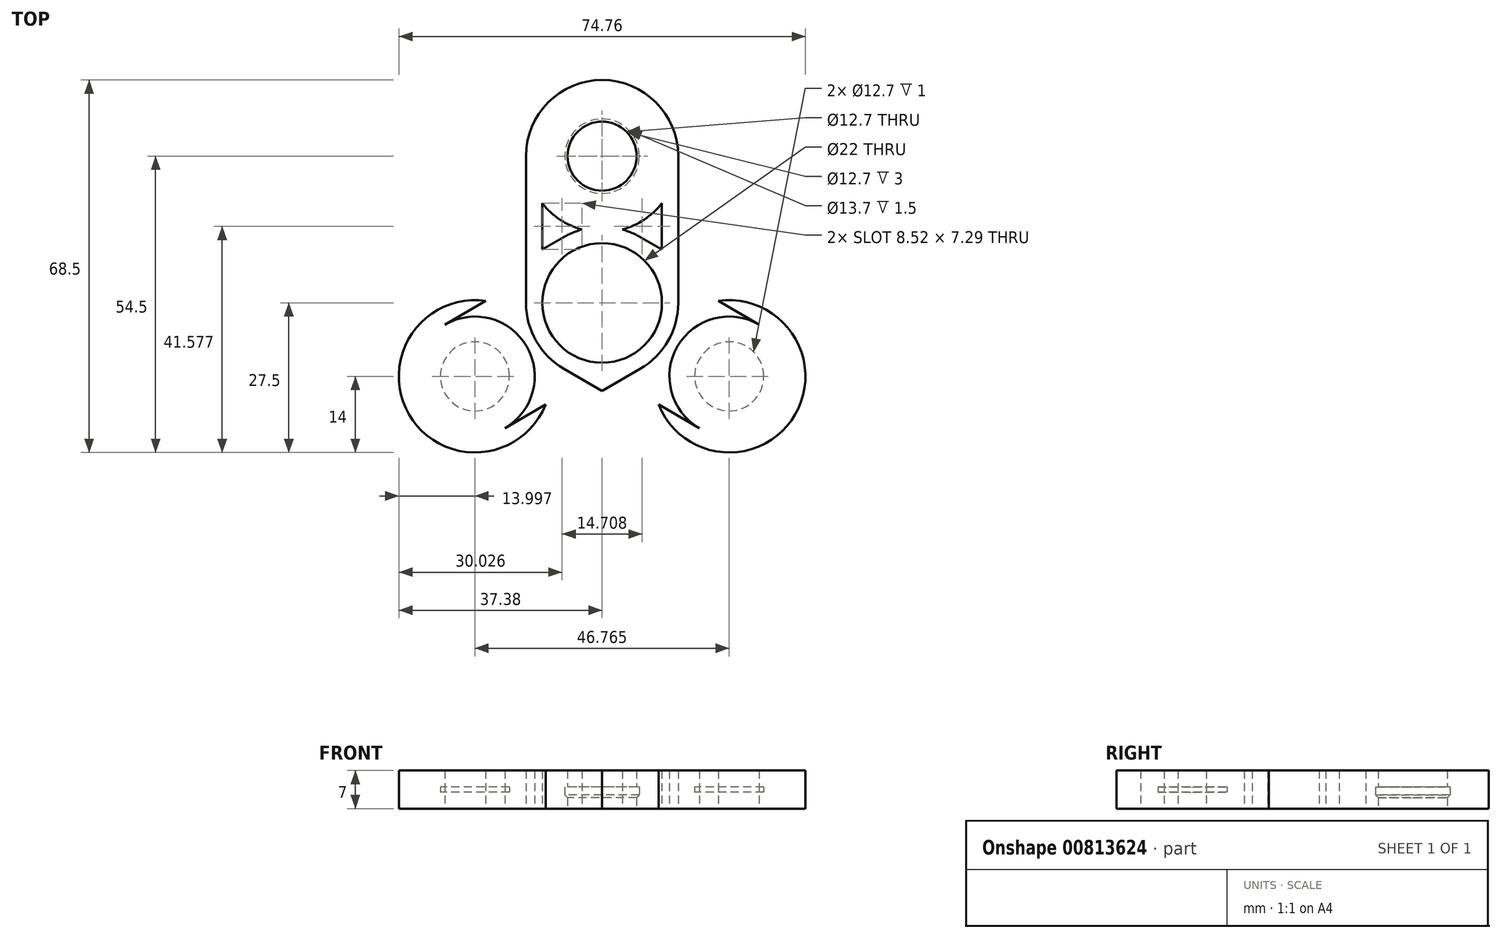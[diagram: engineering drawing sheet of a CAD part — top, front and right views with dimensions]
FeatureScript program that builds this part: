
annotation { "Feature Type Name" : "Feature", "Feature Type Description" : "" }
export const myFeature = defineFeature(function(context is Context, id is Id, definition is map)
    precondition{}
    {
        {
            var Q0;
            Q0=qCreatedBy(makeId("Top.planeOp"),FACE);
            var sketch = newSketch(context, id + "F0", { "sketchPlane" : qUnion([Q0])});
            skCircle(sketch, "E0", {"center": v(0, 0) * mm, "radius": 11 * mm});
            skCircle(sketch, "E1", {"center": v(0, 27) * mm, "radius": 11 * mm});
            skLineSegment(sketch, "E2", {"start": v(0, 0) * mm, "end": v(-42.66, -24.63) * mm, "construction": true});
            skLineSegment(sketch, "E3", {"start": v(0, 0) * mm, "end": v(40.25, -23.24) * mm, "construction": true});
            skCircle(sketch, "E4.MirrorC", {"center": v(23.38, -13.5) * mm, "radius": 11 * mm});
            skCircle(sketch, "E5.MirrorC", {"center": v(-23.38, -13.5) * mm, "radius": 11 * mm});
            skCircle(sketch, "E6", {"center": v(0, 0) * mm, "radius": 14 * mm});
            skCircle(sketch, "E7", {"center": v(0, 27) * mm, "radius": 14 * mm});
            skCircle(sketch, "E8.MirrorC", {"center": v(23.38, -13.5) * mm, "radius": 14 * mm});
            skCircle(sketch, "E9.MirrorC", {"center": v(-23.38, -13.5) * mm, "radius": 14 * mm});
            skLineSegment(sketch, "E10", {"start": v(-30.38, -1.38) * mm, "end": v(-7, 12.12) * mm});
            skLineSegment(sketch, "E11", {"start": v(-16.38, -25.62) * mm, "end": v(7, -12.12) * mm});
            skCircle(sketch, "E12", {"center": v(0, 27) * mm, "radius": 6.35 * mm});
            skCircle(sketch, "E13.MirrorC", {"center": v(23.38, -13.5) * mm, "radius": 6.35 * mm});
            skCircle(sketch, "E14.MirrorC", {"center": v(-23.38, -13.5) * mm, "radius": 6.35 * mm});
            skLineSegment(sketch, "E15.MirrorCS", {"start": v(30.38, -1.38) * mm, "end": v(7, 12.12) * mm});
            skLineSegment(sketch, "E16.MirrorCS", {"start": v(16.38, -25.62) * mm, "end": v(-7, -12.12) * mm});
            skLineSegment(sketch, "E17.MirrorCS", {"start": v(-14, 27) * mm, "end": v(-14, 0) * mm});
            skLineSegment(sketch, "E18.MirrorCS", {"start": v(14, 27) * mm, "end": v(14, 0) * mm});
            skLineSegment(sketch, "E19", {"start": v(-28.88, -3.97) * mm, "end": v(-5.5, 9.53) * mm});
            skLineSegment(sketch, "E20.MirrorCS", {"start": v(-17.88, -23.03) * mm, "end": v(5.5, -9.53) * mm});
            skLineSegment(sketch, "E21.MirrorCS", {"start": v(-11, 27) * mm, "end": v(-11, 0) * mm});
            skLineSegment(sketch, "E22.MirrorCS", {"start": v(11, 27) * mm, "end": v(11, 0) * mm});
            skLineSegment(sketch, "E23.MirrorCS", {"start": v(28.88, -3.97) * mm, "end": v(5.5, 9.53) * mm});
            skLineSegment(sketch, "E24.MirrorCS", {"start": v(17.88, -23.03) * mm, "end": v(-5.5, -9.53) * mm});
            skCircle(sketch, "E25", {"center": v(0, 27) * mm, "radius": 6.85 * mm});
            skCircle(sketch, "E26.MirrorC", {"center": v(23.38, -13.5) * mm, "radius": 6.85 * mm});
            skCircle(sketch, "E27.MirrorC", {"center": v(-23.38, -13.5) * mm, "radius": 6.85 * mm});
            skSolve(sketch);
        }
        {
            var Q0;
            {var subQ5=sQuery(id+"F0.wireOp",EDGE,"E21.MirrorCS");var subQ7=sQuery(id+"F0.wireOp",EDGE,"E1");var subQ8=makeQuery(id+"F0.imprint","INTERSECT",VERTEX,{"derivedFrom":[subQ7,subQ5]});Q0=makeQuery(id+"F0.imprint","IMPRINT",FACE,{"disambiguationData":[TD([[makeQuery(id+"F0.imprint","IMPRINT",EDGE,{"disambiguationData":[TD([[subQ8,1.0]])],"derivedFrom":subQ7}),-1.0]])]});}
            var Q1;
            Q1=makeQuery(id+"F0.imprint","IMPRINT",FACE,{"disambiguationData":[TD([[makeQuery(id+"F0.imprint","IMPRINT",EDGE,{"derivedFrom":sQuery(id+"F0.wireOp",EDGE,"E12")}),-1.0]])]});
            var Q2;
            {var subQ0=sQuery(id+"F0.wireOp",EDGE,"E21.MirrorCS");var subQ1=sQuery(id+"F0.wireOp",EDGE,"E1");var subQ2=makeQuery(id+"F0.imprint","INTERSECT",VERTEX,{"derivedFrom":[subQ1,subQ0]});Q2=makeQuery(id+"F0.imprint","IMPRINT",FACE,{"disambiguationData":[TD([[makeQuery(id+"F0.imprint","IMPRINT",EDGE,{"disambiguationData":[TD([[subQ2,-1.0]])],"derivedFrom":subQ1}),-1.0]])]});}
            var Q3;
            {var subQ0=sQuery(id+"F0.wireOp",EDGE,"E17.MirrorCS");var subQ1=sQuery(id+"F0.wireOp",EDGE,"E7");var subQ2=makeQuery(id+"F0.imprint","INTERSECT",VERTEX,{"derivedFrom":[subQ1,subQ0]});Q3=makeQuery(id+"F0.imprint","IMPRINT",FACE,{"disambiguationData":[TD([[makeQuery(id+"F0.imprint","IMPRINT",EDGE,{"disambiguationData":[TD([[subQ2,-1.0]])],"derivedFrom":subQ1}),-1.0]])]});}
            var Q4;
            {var subQ0=sQuery(id+"F0.wireOp",EDGE,"E10");var subQ1=sQuery(id+"F0.wireOp",EDGE,"E9.MirrorC");var subQ2=makeQuery(id+"F0.imprint","INTERSECT",VERTEX,{"derivedFrom":[subQ1,subQ0]});Q4=makeQuery(id+"F0.imprint","IMPRINT",FACE,{"disambiguationData":[TD([[makeQuery(id+"F0.imprint","IMPRINT",EDGE,{"disambiguationData":[TD([[subQ2,-1.0]])],"derivedFrom":subQ1}),1.0]])]});}
            var Q5;
            {var subQ2=sQuery(id+"F0.wireOp",EDGE,"E19");var subQ5=sQuery(id+"F0.wireOp",EDGE,"E5.MirrorC");var subQ6=makeQuery(id+"F0.imprint","INTERSECT",VERTEX,{"derivedFrom":[subQ5,subQ2]});Q5=makeQuery(id+"F0.imprint","IMPRINT",FACE,{"disambiguationData":[TD([[makeQuery(id+"F0.imprint","IMPRINT",EDGE,{"disambiguationData":[TD([[subQ6,1.0]])],"derivedFrom":subQ5}),1.0]])]});}
            var Q6;
            Q6=makeQuery(id+"F0.imprint","IMPRINT",FACE,{"disambiguationData":[TD([[makeQuery(id+"F0.imprint","IMPRINT",EDGE,{"derivedFrom":sQuery(id+"F0.wireOp",EDGE,"E14.MirrorC")}),1.0]])]});
            var Q7;
            {var subQ0=sQuery(id+"F0.wireOp",EDGE,"E19");var subQ1=sQuery(id+"F0.wireOp",EDGE,"E5.MirrorC");var subQ2=makeQuery(id+"F0.imprint","INTERSECT",VERTEX,{"derivedFrom":[subQ1,subQ0]});Q7=makeQuery(id+"F0.imprint","IMPRINT",FACE,{"disambiguationData":[TD([[makeQuery(id+"F0.imprint","IMPRINT",EDGE,{"disambiguationData":[TD([[subQ2,-1.0]])],"derivedFrom":subQ1}),1.0]])]});}
            var Q8;
            {var subQ0=sQuery(id+"F0.wireOp",EDGE,"E11");var subQ1=sQuery(id+"F0.wireOp",EDGE,"E9.MirrorC");var subQ2=makeQuery(id+"F0.imprint","INTERSECT",VERTEX,{"derivedFrom":[subQ1,subQ0]});Q8=makeQuery(id+"F0.imprint","IMPRINT",FACE,{"disambiguationData":[TD([[makeQuery(id+"F0.imprint","IMPRINT",EDGE,{"disambiguationData":[TD([[subQ2,1.0]])],"derivedFrom":subQ1}),1.0]])]});}
            var Q9;
            {var subQ0=sQuery(id+"F0.wireOp",EDGE,"E16.MirrorCS");var subQ1=sQuery(id+"F0.wireOp",EDGE,"E8.MirrorC");var subQ2=makeQuery(id+"F0.imprint","INTERSECT",VERTEX,{"derivedFrom":[subQ1,subQ0]});Q9=makeQuery(id+"F0.imprint","IMPRINT",FACE,{"disambiguationData":[TD([[makeQuery(id+"F0.imprint","IMPRINT",EDGE,{"disambiguationData":[TD([[subQ2,-1.0]])],"derivedFrom":subQ1}),1.0]])]});}
            var Q10;
            {var subQ2=sQuery(id+"F0.wireOp",EDGE,"E23.MirrorCS");var subQ7=sQuery(id+"F0.wireOp",EDGE,"E4.MirrorC");var subQ8=makeQuery(id+"F0.imprint","INTERSECT",VERTEX,{"derivedFrom":[subQ7,subQ2]});Q10=makeQuery(id+"F0.imprint","IMPRINT",FACE,{"disambiguationData":[TD([[makeQuery(id+"F0.imprint","IMPRINT",EDGE,{"disambiguationData":[TD([[subQ8,-1.0]])],"derivedFrom":subQ7}),1.0]])]});}
            var Q11;
            {var subQ0=sQuery(id+"F0.wireOp",EDGE,"E23.MirrorCS");var subQ1=sQuery(id+"F0.wireOp",EDGE,"E4.MirrorC");var subQ2=makeQuery(id+"F0.imprint","INTERSECT",VERTEX,{"derivedFrom":[subQ1,subQ0]});Q11=makeQuery(id+"F0.imprint","IMPRINT",FACE,{"disambiguationData":[TD([[makeQuery(id+"F0.imprint","IMPRINT",EDGE,{"disambiguationData":[TD([[subQ2,1.0]])],"derivedFrom":subQ1}),1.0]])]});}
            var Q12;
            Q12=makeQuery(id+"F0.imprint","IMPRINT",FACE,{"disambiguationData":[TD([[makeQuery(id+"F0.imprint","IMPRINT",EDGE,{"derivedFrom":sQuery(id+"F0.wireOp",EDGE,"E13.MirrorC")}),1.0]])]});
            var Q13;
            {var subQ0=sQuery(id+"F0.wireOp",EDGE,"E15.MirrorCS");var subQ1=sQuery(id+"F0.wireOp",EDGE,"E8.MirrorC");var subQ2=makeQuery(id+"F0.imprint","INTERSECT",VERTEX,{"derivedFrom":[subQ1,subQ0]});Q13=makeQuery(id+"F0.imprint","IMPRINT",FACE,{"disambiguationData":[TD([[makeQuery(id+"F0.imprint","IMPRINT",EDGE,{"disambiguationData":[TD([[subQ2,1.0]])],"derivedFrom":subQ1}),1.0]])]});}
            var Q14;
            {var subQ0=sQuery(id+"F0.wireOp",EDGE,"E18.MirrorCS");var subQ1=sQuery(id+"F0.wireOp",EDGE,"E7");var subQ2=makeQuery(id+"F0.imprint","INTERSECT",VERTEX,{"derivedFrom":[subQ1,subQ0]});Q14=makeQuery(id+"F0.imprint","IMPRINT",FACE,{"disambiguationData":[TD([[makeQuery(id+"F0.imprint","IMPRINT",EDGE,{"disambiguationData":[TD([[subQ2,1.0]])],"derivedFrom":subQ1}),-1.0]])]});}
            var Q15;
            {var subQ5=sQuery(id+"F0.wireOp",EDGE,"E19");var subQ8=sQuery(id+"F0.wireOp",EDGE,"E0");var subQ13=makeQuery(id+"F0.imprint","INTERSECT",VERTEX,{"derivedFrom":[subQ8,subQ5]});Q15=makeQuery(id+"F0.imprint","IMPRINT",FACE,{"disambiguationData":[TD([[makeQuery(id+"F0.imprint","IMPRINT",EDGE,{"disambiguationData":[TD([[subQ13,1.0]])],"derivedFrom":subQ8}),-1.0]])]});}
            var Q16;
            {var subQ7=sQuery(id+"F0.wireOp",EDGE,"E20.MirrorCS");var subQ8=sQuery(id+"F0.wireOp",EDGE,"E0");var subQ9=makeQuery(id+"F0.imprint","INTERSECT",VERTEX,{"derivedFrom":[subQ8,subQ7]});Q16=makeQuery(id+"F0.imprint","IMPRINT",FACE,{"disambiguationData":[TD([[makeQuery(id+"F0.imprint","IMPRINT",EDGE,{"disambiguationData":[TD([[subQ9,-1.0]])],"derivedFrom":subQ8}),-1.0]])]});}
            var Q17;
            {var subQ5=sQuery(id+"F0.wireOp",EDGE,"E0");var subQ11=sQuery(id+"F0.wireOp",EDGE,"E21.MirrorCS");var subQ12=makeQuery(id+"F0.imprint","INTERSECT",VERTEX,{"derivedFrom":[subQ5,subQ11]});Q17=makeQuery(id+"F0.imprint","IMPRINT",FACE,{"disambiguationData":[TD([[makeQuery(id+"F0.imprint","IMPRINT",EDGE,{"disambiguationData":[TD([[subQ12,-1.0]])],"derivedFrom":subQ5}),-1.0]])]});}
            var Q18;
            {var subQ1=sQuery(id+"F0.wireOp",EDGE,"E6");var subQ7=sQuery(id+"F0.wireOp",EDGE,"E21.MirrorCS");var subQ9=makeQuery(id+"F0.imprint","INTERSECT",VERTEX,{"derivedFrom":[subQ1,subQ7]});Q18=makeQuery(id+"F0.imprint","IMPRINT",FACE,{"disambiguationData":[TD([[makeQuery(id+"F0.imprint","IMPRINT",EDGE,{"disambiguationData":[TD([[subQ9,-1.0]])],"derivedFrom":subQ1}),-1.0]])]});}
            var Q19;
            {var subQ0=sQuery(id+"F0.wireOp",EDGE,"E21.MirrorCS");var subQ1=sQuery(id+"F0.wireOp",EDGE,"E6");var subQ2=makeQuery(id+"F0.imprint","INTERSECT",VERTEX,{"derivedFrom":[subQ1,subQ0]});Q19=makeQuery(id+"F0.imprint","IMPRINT",FACE,{"disambiguationData":[TD([[makeQuery(id+"F0.imprint","IMPRINT",EDGE,{"disambiguationData":[TD([[subQ2,-1.0]])],"derivedFrom":subQ1}),1.0]])]});}
            var Q20;
            {var subQ0=sQuery(id+"F0.wireOp",EDGE,"E10");var subQ1=sQuery(id+"F0.wireOp",EDGE,"E6");var subQ2=makeQuery(id+"F0.imprint","INTERSECT",VERTEX,{"derivedFrom":[subQ1,subQ0]});Q20=makeQuery(id+"F0.imprint","IMPRINT",FACE,{"disambiguationData":[TD([[makeQuery(id+"F0.imprint","IMPRINT",EDGE,{"disambiguationData":[TD([[subQ2,-1.0]])],"derivedFrom":subQ1}),-1.0]])]});}
            var Q21;
            {var subQ0=sQuery(id+"F0.wireOp",EDGE,"E17.MirrorCS");var subQ1=sQuery(id+"F0.wireOp",EDGE,"E6");var subQ2=makeQuery(id+"F0.imprint","INTERSECT",VERTEX,{"derivedFrom":[subQ1,subQ0]});Q21=makeQuery(id+"F0.imprint","IMPRINT",FACE,{"disambiguationData":[TD([[makeQuery(id+"F0.imprint","IMPRINT",EDGE,{"disambiguationData":[TD([[subQ2,1.0]])],"derivedFrom":subQ1}),-1.0]])]});}
            var Q22;
            {var subQ0=sQuery(id+"F0.wireOp",EDGE,"E19");var subQ1=sQuery(id+"F0.wireOp",EDGE,"E0");var subQ2=makeQuery(id+"F0.imprint","INTERSECT",VERTEX,{"derivedFrom":[subQ1,subQ0]});Q22=makeQuery(id+"F0.imprint","IMPRINT",FACE,{"disambiguationData":[TD([[makeQuery(id+"F0.imprint","IMPRINT",EDGE,{"disambiguationData":[TD([[subQ2,-1.0]])],"derivedFrom":subQ1}),-1.0]])]});}
            var Q23;
            {var subQ0=sQuery(id+"F0.wireOp",EDGE,"E15.MirrorCS");var subQ1=sQuery(id+"F0.wireOp",EDGE,"E6");var subQ2=makeQuery(id+"F0.imprint","INTERSECT",VERTEX,{"derivedFrom":[subQ1,subQ0]});Q23=makeQuery(id+"F0.imprint","IMPRINT",FACE,{"disambiguationData":[TD([[makeQuery(id+"F0.imprint","IMPRINT",EDGE,{"disambiguationData":[TD([[subQ2,1.0]])],"derivedFrom":subQ1}),-1.0]])]});}
            var Q24;
            {var subQ1=sQuery(id+"F0.wireOp",EDGE,"E6");var subQ7=sQuery(id+"F0.wireOp",EDGE,"E23.MirrorCS");var subQ9=makeQuery(id+"F0.imprint","INTERSECT",VERTEX,{"derivedFrom":[subQ1,subQ7]});Q24=makeQuery(id+"F0.imprint","IMPRINT",FACE,{"disambiguationData":[TD([[makeQuery(id+"F0.imprint","IMPRINT",EDGE,{"disambiguationData":[TD([[subQ9,-1.0]])],"derivedFrom":subQ1}),-1.0]])]});}
            var Q25;
            {var subQ0=sQuery(id+"F0.wireOp",EDGE,"E23.MirrorCS");var subQ1=sQuery(id+"F0.wireOp",EDGE,"E6");var subQ2=makeQuery(id+"F0.imprint","INTERSECT",VERTEX,{"derivedFrom":[subQ1,subQ0]});Q25=makeQuery(id+"F0.imprint","IMPRINT",FACE,{"disambiguationData":[TD([[makeQuery(id+"F0.imprint","IMPRINT",EDGE,{"disambiguationData":[TD([[subQ2,-1.0]])],"derivedFrom":subQ1}),1.0]])]});}
            var Q26;
            {var subQ0=sQuery(id+"F0.wireOp",EDGE,"E22.MirrorCS");var subQ1=sQuery(id+"F0.wireOp",EDGE,"E0");var subQ2=makeQuery(id+"F0.imprint","INTERSECT",VERTEX,{"derivedFrom":[subQ1,subQ0]});Q26=makeQuery(id+"F0.imprint","IMPRINT",FACE,{"disambiguationData":[TD([[makeQuery(id+"F0.imprint","IMPRINT",EDGE,{"disambiguationData":[TD([[subQ2,-1.0]])],"derivedFrom":subQ1}),-1.0]])]});}
            var Q27;
            {var subQ0=sQuery(id+"F0.wireOp",EDGE,"E20.MirrorCS");var subQ1=sQuery(id+"F0.wireOp",EDGE,"E6");var subQ2=makeQuery(id+"F0.imprint","INTERSECT",VERTEX,{"derivedFrom":[subQ1,subQ0]});Q27=makeQuery(id+"F0.imprint","IMPRINT",FACE,{"disambiguationData":[TD([[makeQuery(id+"F0.imprint","IMPRINT",EDGE,{"disambiguationData":[TD([[subQ2,-1.0]])],"derivedFrom":subQ1}),-1.0]])]});}
            var Q28;
            {var subQ0=sQuery(id+"F0.wireOp",EDGE,"E20.MirrorCS");var subQ1=sQuery(id+"F0.wireOp",EDGE,"E6");var subQ2=makeQuery(id+"F0.imprint","INTERSECT",VERTEX,{"derivedFrom":[subQ1,subQ0]});Q28=makeQuery(id+"F0.imprint","IMPRINT",FACE,{"disambiguationData":[TD([[makeQuery(id+"F0.imprint","IMPRINT",EDGE,{"disambiguationData":[TD([[subQ2,-1.0]])],"derivedFrom":subQ1}),1.0]])]});}
            var Q29;
            {var subQ0=sQuery(id+"F0.wireOp",EDGE,"E11");var subQ1=sQuery(id+"F0.wireOp",EDGE,"E6");var subQ2=makeQuery(id+"F0.imprint","INTERSECT",VERTEX,{"derivedFrom":[subQ1,subQ0]});Q29=makeQuery(id+"F0.imprint","IMPRINT",FACE,{"disambiguationData":[TD([[makeQuery(id+"F0.imprint","IMPRINT",EDGE,{"disambiguationData":[TD([[subQ2,1.0]])],"derivedFrom":subQ1}),-1.0]])]});}
            var Q30;
            {var subQ0=sQuery(id+"F0.wireOp",EDGE,"E18.MirrorCS");var subQ1=sQuery(id+"F0.wireOp",EDGE,"E6");var subQ2=makeQuery(id+"F0.imprint","INTERSECT",VERTEX,{"derivedFrom":[subQ1,subQ0]});Q30=makeQuery(id+"F0.imprint","IMPRINT",FACE,{"disambiguationData":[TD([[makeQuery(id+"F0.imprint","IMPRINT",EDGE,{"disambiguationData":[TD([[subQ2,-1.0]])],"derivedFrom":subQ1}),-1.0]])]});}
            var Q31;
            {var subQ0=sQuery(id+"F0.wireOp",EDGE,"E20.MirrorCS");var subQ1=sQuery(id+"F0.wireOp",EDGE,"E0");var subQ2=makeQuery(id+"F0.imprint","INTERSECT",VERTEX,{"derivedFrom":[subQ1,subQ0]});Q31=makeQuery(id+"F0.imprint","IMPRINT",FACE,{"disambiguationData":[TD([[makeQuery(id+"F0.imprint","IMPRINT",EDGE,{"disambiguationData":[TD([[subQ2,1.0]])],"derivedFrom":subQ1}),-1.0]])]});}
            var Q32;
            {var subQ0=sQuery(id+"F0.wireOp",EDGE,"E16.MirrorCS");var subQ1=sQuery(id+"F0.wireOp",EDGE,"E6");var subQ2=makeQuery(id+"F0.imprint","INTERSECT",VERTEX,{"derivedFrom":[subQ1,subQ0]});Q32=makeQuery(id+"F0.imprint","IMPRINT",FACE,{"disambiguationData":[TD([[makeQuery(id+"F0.imprint","IMPRINT",EDGE,{"disambiguationData":[TD([[subQ2,-1.0]])],"derivedFrom":subQ1}),-1.0]])]});}
            var Q33;
            {var subQ0=sQuery(id+"F0.wireOp",EDGE,"E7");var subQ1=sQuery(id+"F0.wireOp",EDGE,"E6");var subQ2=makeQuery(id+"F0.imprint","INTERSECT",VERTEX,{"disambiguationData":[OD(0.0)],"derivedFrom":[subQ1,subQ0]});Q33=makeQuery(id+"F0.imprint","IMPRINT",FACE,{"disambiguationData":[TD([[makeQuery(id+"F0.imprint","IMPRINT",EDGE,{"disambiguationData":[TD([[subQ2,-1.0]])],"derivedFrom":subQ1}),1.0]])]});}
            var Q34;
            {var subQ0=sQuery(id+"F0.wireOp",EDGE,"E9.MirrorC");var subQ1=sQuery(id+"F0.wireOp",EDGE,"E6");var subQ2=makeQuery(id+"F0.imprint","INTERSECT",VERTEX,{"disambiguationData":[OD(0.0)],"derivedFrom":[subQ1,subQ0]});Q34=makeQuery(id+"F0.imprint","IMPRINT",FACE,{"disambiguationData":[TD([[makeQuery(id+"F0.imprint","IMPRINT",EDGE,{"disambiguationData":[TD([[subQ2,-1.0]])],"derivedFrom":subQ1}),1.0]])]});}
            var Q35;
            {var subQ0=sQuery(id+"F0.wireOp",EDGE,"E8.MirrorC");var subQ1=sQuery(id+"F0.wireOp",EDGE,"E6");var subQ2=makeQuery(id+"F0.imprint","INTERSECT",VERTEX,{"disambiguationData":[OD(0.0)],"derivedFrom":[subQ1,subQ0]});Q35=makeQuery(id+"F0.imprint","IMPRINT",FACE,{"disambiguationData":[TD([[makeQuery(id+"F0.imprint","IMPRINT",EDGE,{"disambiguationData":[TD([[subQ2,-1.0]])],"derivedFrom":subQ1}),1.0]])]});}
            var Q36;
            Q36=makeQuery(id+"F0.imprint","IMPRINT",FACE,{"disambiguationData":[TD([[makeQuery(id+"F0.imprint","IMPRINT",EDGE,{"derivedFrom":sQuery(id+"F0.wireOp",EDGE,"E25")}),-1.0]])]});
            var Q37;
            Q37=makeQuery(id+"F0.imprint","IMPRINT",FACE,{"disambiguationData":[TD([[makeQuery(id+"F0.imprint","IMPRINT",EDGE,{"derivedFrom":sQuery(id+"F0.wireOp",EDGE,"E27.MirrorC")}),1.0]])]});
            var Q38;
            Q38=makeQuery(id+"F0.imprint","IMPRINT",FACE,{"disambiguationData":[TD([[makeQuery(id+"F0.imprint","IMPRINT",EDGE,{"derivedFrom":sQuery(id+"F0.wireOp",EDGE,"E26.MirrorC")}),1.0]])]});
            extrude(context, id + "F1", {"entities" : qUnion([Q0, Q1, Q2, Q3, Q4, Q5, Q6, Q7, Q8, Q9, Q10, Q11, Q12, Q13, Q14, Q15, Q16, Q17, Q18, Q19, Q20, Q21, Q22, Q23, Q24, Q25, Q26, Q27, Q28, Q29, Q30, Q31, Q32, Q33, Q34, Q35, Q36, Q37, Q38]), "endBound" : BoundingType.SYMMETRIC, "depth" : 7 * mm, "offsetDistance" : 25 * mm});
        }
        {
            var Q0;
            Q0=makeQuery(id+"F0.imprint","IMPRINT",FACE,{"disambiguationData":[TD([[makeQuery(id+"F0.imprint","IMPRINT",EDGE,{"derivedFrom":sQuery(id+"F0.wireOp",EDGE,"E12")}),-1.0]])]});
            var Q1;
            Q1=makeQuery(id+"F0.imprint","IMPRINT",FACE,{"disambiguationData":[TD([[makeQuery(id+"F0.imprint","IMPRINT",EDGE,{"derivedFrom":sQuery(id+"F0.wireOp",EDGE,"E14.MirrorC")}),1.0]])]});
            var Q2;
            Q2=makeQuery(id+"F0.imprint","IMPRINT",FACE,{"disambiguationData":[TD([[makeQuery(id+"F0.imprint","IMPRINT",EDGE,{"derivedFrom":sQuery(id+"F0.wireOp",EDGE,"E13.MirrorC")}),1.0]])]});
            extrude(context, id + "F2", {"entities" : qUnion([Q0, Q1, Q2]), "operationType" : NewBodyOperationType.REMOVE, "endBound" : BoundingType.SYMMETRIC, "depth" : 1 * mm, "offsetDistance" : 25 * mm});
        }
        {
            var Q0;
            Q0=makeQuery(id+"F2.boolean.opBoolean","COPY",EDGE,{"derivedFrom":makeQuery(id+"F2.opExtrude","CAP_EDGE",EDGE,{"disambiguationData":[OSD([sQuery(id+"F0.wireOp",EDGE,"E12")])],"isStart":false})});
            var Q1;
            Q1=makeQuery(id+"F2.boolean.opBoolean","COPY",EDGE,{"derivedFrom":makeQuery(id+"F2.opExtrude","CAP_EDGE",EDGE,{"disambiguationData":[OSD([sQuery(id+"F0.wireOp",EDGE,"E12")])],"isStart":true})});
            var Q2;
            Q2=makeQuery(id+"F2.boolean.opBoolean","COPY",EDGE,{"derivedFrom":makeQuery(id+"F2.opExtrude","CAP_EDGE",EDGE,{"disambiguationData":[OSD([sQuery(id+"F0.wireOp",EDGE,"E13.MirrorC")])],"isStart":false})});
            var Q3;
            Q3=makeQuery(id+"F2.boolean.opBoolean","COPY",EDGE,{"derivedFrom":makeQuery(id+"F2.opExtrude","CAP_EDGE",EDGE,{"disambiguationData":[OSD([sQuery(id+"F0.wireOp",EDGE,"E13.MirrorC")])],"isStart":true})});
            var Q4;
            Q4=makeQuery(id+"F2.boolean.opBoolean","COPY",EDGE,{"derivedFrom":makeQuery(id+"F2.opExtrude","CAP_EDGE",EDGE,{"disambiguationData":[OSD([sQuery(id+"F0.wireOp",EDGE,"E14.MirrorC")])],"isStart":true})});
            var Q5;
            Q5=makeQuery(id+"F2.boolean.opBoolean","COPY",EDGE,{"derivedFrom":makeQuery(id+"F2.opExtrude","CAP_EDGE",EDGE,{"disambiguationData":[OSD([sQuery(id+"F0.wireOp",EDGE,"E14.MirrorC")])],"isStart":false})});
            chamfer(context, id + "F3", {"entities" : qUnion([Q0, Q1, Q2, Q3, Q4, Q5]), "width" : 1 * mm, "tangentPropagation" : true});
        }
    });
